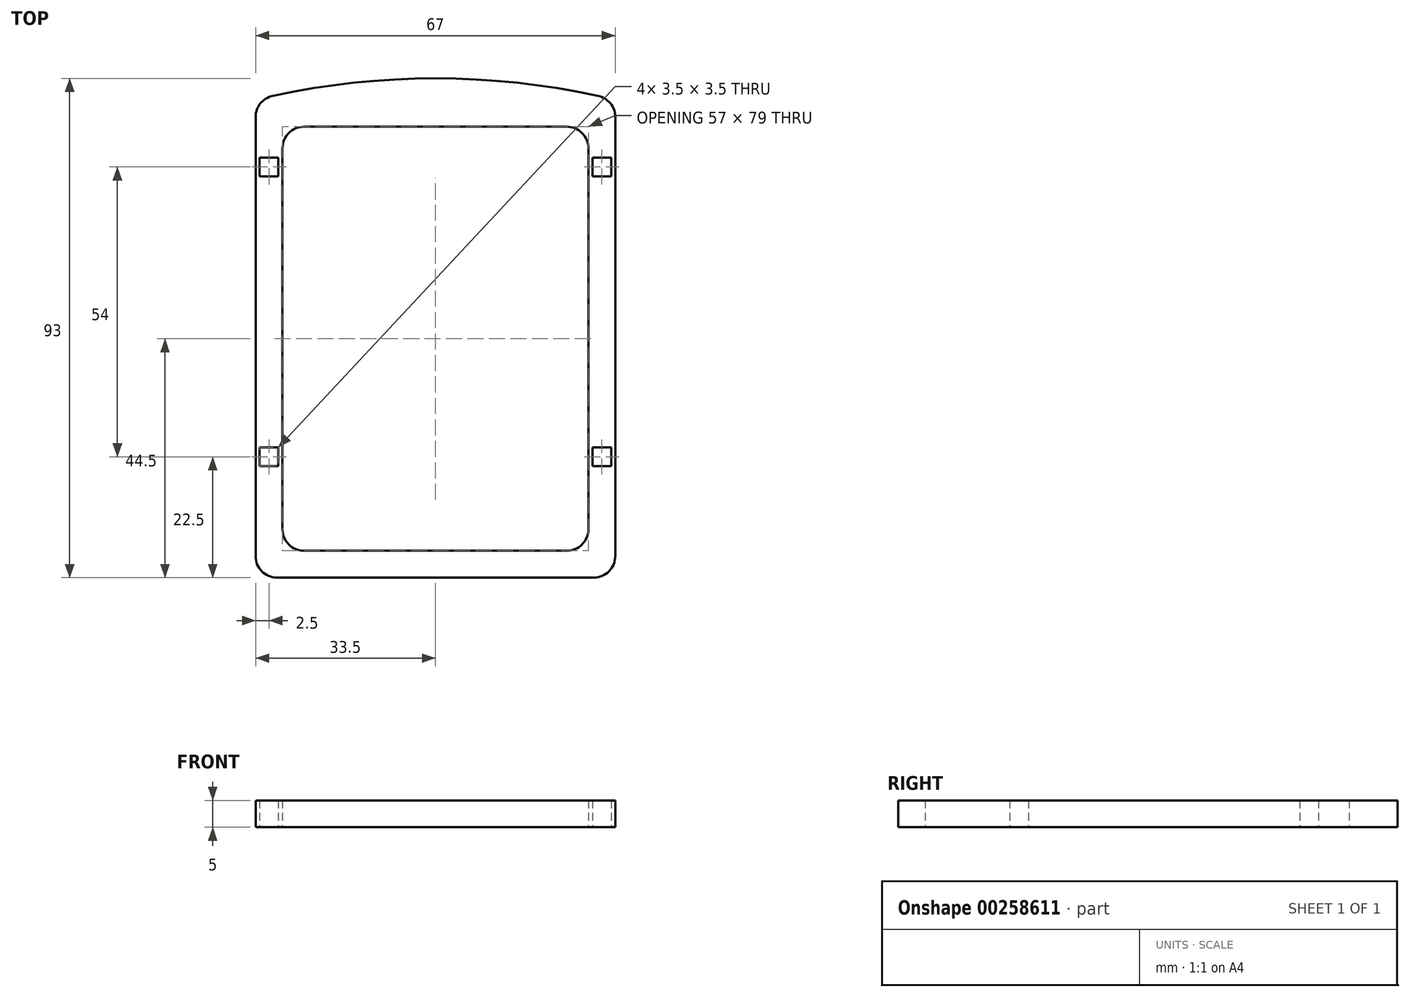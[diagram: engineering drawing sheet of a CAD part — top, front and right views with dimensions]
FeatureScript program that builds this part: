
annotation { "Feature Type Name" : "Feature", "Feature Type Description" : "" }
export const myFeature = defineFeature(function(context is Context, id is Id, definition is map)
    precondition{}
    {
        {
            var Q0;
            Q0=qCreatedBy(makeId("Top.planeOp"),FACE);
            var sketch = newSketch(context, id + "F0", { "sketchPlane" : qUnion([Q0])});
            skLineSegment(sketch, "E0.bottom", {"start": v(33.5, 44.5) * mm, "end": v(-33.5, 44.5) * mm});
            skLineSegment(sketch, "E0.top", {"start": v(33.5, -44.5) * mm, "end": v(-33.5, -44.5) * mm});
            skLineSegment(sketch, "E0.left", {"start": v(33.5, 44.5) * mm, "end": v(33.5, -44.5) * mm});
            skLineSegment(sketch, "E0.right", {"start": v(-33.5, 44.5) * mm, "end": v(-33.5, -44.5) * mm});
            skPoint(sketch, "E0.middle", {"position": v(0, 0) * mm});
            skLineSegment(sketch, "E1.0", {"start": v(-28.5, 39.5) * mm, "end": v(-28.5, -39.5) * mm});
            skLineSegment(sketch, "E1.1", {"start": v(28.5, 39.5) * mm, "end": v(-28.5, 39.5) * mm});
            skLineSegment(sketch, "E1.2", {"start": v(28.5, 39.5) * mm, "end": v(28.5, -39.5) * mm});
            skLineSegment(sketch, "E1.3", {"start": v(28.5, -39.5) * mm, "end": v(-28.5, -39.5) * mm});
            skLineSegment(sketch, "E2", {"start": v(0, -44.5) * mm, "end": v(0, 48.5) * mm, "construction": true});
            skPoint(sketch, "E2.endSnap0", {"position": v(0, -39.5) * mm});
            skArc(sketch, "E3", {"start": v(33.5, 44.5) * mm, "mid": v(0, 48.5) * mm, "end": v(-33.5, 44.5) * mm});
            skLineSegment(sketch, "E4.bottom", {"start": v(-28.5, 39.5) * mm, "end": v(-33.5, 39.5) * mm, "construction": true});
            skLineSegment(sketch, "E4.top", {"start": v(-28.5, 34.5) * mm, "end": v(-33.5, 34.5) * mm, "construction": true});
            skLineSegment(sketch, "E4.left", {"start": v(-28.5, 39.5) * mm, "end": v(-28.5, 34.5) * mm, "construction": true});
            skLineSegment(sketch, "E4.right", {"start": v(-33.5, 39.5) * mm, "end": v(-33.5, 34.5) * mm, "construction": true});
            skLineSegment(sketch, "E5.bottom", {"start": v(28.5, 39.5) * mm, "end": v(33.5, 39.5) * mm, "construction": true});
            skLineSegment(sketch, "E5.top", {"start": v(28.5, 34.5) * mm, "end": v(33.5, 34.5) * mm, "construction": true});
            skLineSegment(sketch, "E5.left", {"start": v(28.5, 39.5) * mm, "end": v(28.5, 34.5) * mm, "construction": true});
            skLineSegment(sketch, "E5.right", {"start": v(33.5, 39.5) * mm, "end": v(33.5, 34.5) * mm, "construction": true});
            skLineSegment(sketch, "E6.bottom", {"start": v(-33.5, 34.5) * mm, "end": v(-28.5, 34.5) * mm, "construction": true});
            skLineSegment(sketch, "E6.top", {"start": v(-33.5, 29.5) * mm, "end": v(-28.5, 29.5) * mm, "construction": true});
            skLineSegment(sketch, "E6.left", {"start": v(-33.5, 34.5) * mm, "end": v(-33.5, 29.5) * mm, "construction": true});
            skLineSegment(sketch, "E6.right", {"start": v(-28.5, 34.5) * mm, "end": v(-28.5, 29.5) * mm, "construction": true});
            skLineSegment(sketch, "E7.top", {"start": v(28.5, 29.5) * mm, "end": v(33.5, 29.5) * mm, "construction": true});
            skLineSegment(sketch, "E7.left", {"start": v(28.5, 34.5) * mm, "end": v(28.5, 29.5) * mm, "construction": true});
            skLineSegment(sketch, "E7.right", {"start": v(33.5, 34.5) * mm, "end": v(33.5, 29.5) * mm, "construction": true});
            skLineSegment(sketch, "E8.bottom", {"start": v(-29.25, 33.75) * mm, "end": v(-32.75, 33.75) * mm});
            skLineSegment(sketch, "E8.top", {"start": v(-29.25, 30.25) * mm, "end": v(-32.75, 30.25) * mm});
            skLineSegment(sketch, "E8.left", {"start": v(-29.25, 33.75) * mm, "end": v(-29.25, 30.25) * mm});
            skLineSegment(sketch, "E8.right", {"start": v(-32.75, 33.75) * mm, "end": v(-32.75, 30.25) * mm});
            skPoint(sketch, "E8.middle", {"position": v(-31, 32) * mm});
            skPoint(sketch, "E8.middle.positionSnap0", {"position": v(-28.5, 32) * mm});
            skPoint(sketch, "E8.middle.positionSnap1", {"position": v(-31, 29.5) * mm});
            skPoint(sketch, "E8.centerSnap0", {"position": v(-28.5, 32) * mm});
            skPoint(sketch, "E8.centerSnap1", {"position": v(-31, 29.5) * mm});
            skLineSegment(sketch, "E9.bottom", {"start": v(32.75, 33.75) * mm, "end": v(29.25, 33.75) * mm});
            skLineSegment(sketch, "E9.top", {"start": v(32.75, 30.25) * mm, "end": v(29.25, 30.25) * mm});
            skLineSegment(sketch, "E9.left", {"start": v(32.75, 33.75) * mm, "end": v(32.75, 30.25) * mm});
            skLineSegment(sketch, "E9.right", {"start": v(29.25, 33.75) * mm, "end": v(29.25, 30.25) * mm});
            skPoint(sketch, "E9.middle", {"position": v(31, 32) * mm});
            skPoint(sketch, "E9.middle.positionSnap0", {"position": v(28.5, 32) * mm});
            skPoint(sketch, "E9.middle.positionSnap1", {"position": v(31, 29.5) * mm});
            skPoint(sketch, "E9.centerSnap0", {"position": v(28.5, 32) * mm});
            skPoint(sketch, "E9.centerSnap1", {"position": v(31, 29.5) * mm});
            skLineSegment(sketch, "E10.bottom", {"start": v(-33.5, -44.5) * mm, "end": v(-28.5, -44.5) * mm, "construction": true});
            skLineSegment(sketch, "E10.top", {"start": v(-33.5, -24.5) * mm, "end": v(-28.5, -24.5) * mm, "construction": true});
            skLineSegment(sketch, "E10.left", {"start": v(-33.5, -44.5) * mm, "end": v(-33.5, -24.5) * mm, "construction": true});
            skLineSegment(sketch, "E10.right", {"start": v(-28.5, -44.5) * mm, "end": v(-28.5, -24.5) * mm, "construction": true});
            skLineSegment(sketch, "E11.bottom", {"start": v(33.5, -44.5) * mm, "end": v(28.5, -44.5) * mm, "construction": true});
            skLineSegment(sketch, "E11.top", {"start": v(33.5, -24.5) * mm, "end": v(28.5, -24.5) * mm, "construction": true});
            skLineSegment(sketch, "E11.left", {"start": v(33.5, -44.5) * mm, "end": v(33.5, -24.5) * mm, "construction": true});
            skLineSegment(sketch, "E11.right", {"start": v(28.5, -44.5) * mm, "end": v(28.5, -24.5) * mm, "construction": true});
            skLineSegment(sketch, "E12.bottom", {"start": v(-28.5, -24.5) * mm, "end": v(-33.5, -24.5) * mm, "construction": true});
            skLineSegment(sketch, "E12.top", {"start": v(-28.5, -19.5) * mm, "end": v(-33.5, -19.5) * mm, "construction": true});
            skLineSegment(sketch, "E12.left", {"start": v(-28.5, -24.5) * mm, "end": v(-28.5, -19.5) * mm, "construction": true});
            skLineSegment(sketch, "E12.right", {"start": v(-33.5, -24.5) * mm, "end": v(-33.5, -19.5) * mm, "construction": true});
            skLineSegment(sketch, "E13.bottom", {"start": v(28.5, -24.5) * mm, "end": v(33.5, -24.5) * mm, "construction": true});
            skLineSegment(sketch, "E13.top", {"start": v(28.5, -19.5) * mm, "end": v(33.5, -19.5) * mm, "construction": true});
            skLineSegment(sketch, "E13.left", {"start": v(28.5, -24.5) * mm, "end": v(28.5, -19.5) * mm, "construction": true});
            skLineSegment(sketch, "E13.right", {"start": v(33.5, -24.5) * mm, "end": v(33.5, -19.5) * mm, "construction": true});
            skLineSegment(sketch, "E14.bottom", {"start": v(-29.25, -20.25) * mm, "end": v(-32.75, -20.25) * mm});
            skLineSegment(sketch, "E14.top", {"start": v(-29.25, -23.75) * mm, "end": v(-32.75, -23.75) * mm});
            skLineSegment(sketch, "E14.left", {"start": v(-29.25, -20.25) * mm, "end": v(-29.25, -23.75) * mm});
            skLineSegment(sketch, "E14.right", {"start": v(-32.75, -20.25) * mm, "end": v(-32.75, -23.75) * mm});
            skPoint(sketch, "E14.middle", {"position": v(-31, -22) * mm});
            skPoint(sketch, "E14.middle.positionSnap0", {"position": v(-31, -24.5) * mm});
            skPoint(sketch, "E14.middle.positionSnap1", {"position": v(-28.5, -22) * mm});
            skPoint(sketch, "E14.centerSnap0", {"position": v(-31, -24.5) * mm});
            skPoint(sketch, "E14.centerSnap1", {"position": v(-28.5, -22) * mm});
            skLineSegment(sketch, "E15.bottom", {"start": v(32.75, -20.25) * mm, "end": v(29.25, -20.25) * mm});
            skLineSegment(sketch, "E15.top", {"start": v(32.75, -23.75) * mm, "end": v(29.25, -23.75) * mm});
            skLineSegment(sketch, "E15.left", {"start": v(32.75, -20.25) * mm, "end": v(32.75, -23.75) * mm});
            skLineSegment(sketch, "E15.right", {"start": v(29.25, -20.25) * mm, "end": v(29.25, -23.75) * mm});
            skPoint(sketch, "E15.middle", {"position": v(31, -22) * mm});
            skPoint(sketch, "E15.middle.positionSnap0", {"position": v(28.5, -22) * mm});
            skPoint(sketch, "E15.middle.positionSnap1", {"position": v(31, -24.5) * mm});
            skPoint(sketch, "E15.centerSnap0", {"position": v(28.5, -22) * mm});
            skPoint(sketch, "E15.centerSnap1", {"position": v(31, -24.5) * mm});
            skSolve(sketch);
        }
        {
            var Q0;
            Q0=makeQuery(id+"F0.imprint","IMPRINT",FACE,{"disambiguationData":[TD([[makeQuery(id+"F0.imprint","IMPRINT",EDGE,{"derivedFrom":sQuery(id+"F0.wireOp",EDGE,"E0.bottom")}),1.0]])]});
            var Q1;
            Q1=makeQuery(id+"F0.imprint","IMPRINT",FACE,{"disambiguationData":[TD([[makeQuery(id+"F0.imprint","IMPRINT",EDGE,{"derivedFrom":sQuery(id+"F0.wireOp",EDGE,"E0.bottom")}),-1.0]])]});
            extrude(context, id + "F1", {"entities" : qUnion([Q0, Q1]), "depth" : 5 * mm});
        }
        {
            var Q0;
            Q0=makeQuery(id+"F1.opExtrude","SWEPT_EDGE",EDGE,{"disambiguationData":[OSD([sQuery(id+"F0.wireOp",EDGE,"E0.top"),sQuery(id+"F0.wireOp",EDGE,"E0.right")])]});
            var Q1;
            Q1=makeQuery(id+"F1.opExtrude","SWEPT_EDGE",EDGE,{"disambiguationData":[OSD([sQuery(id+"F0.wireOp",EDGE,"E0.top"),sQuery(id+"F0.wireOp",EDGE,"E0.left")])]});
            var Q2;
            Q2=makeQuery(id+"F1.opExtrude","SWEPT_EDGE",EDGE,{"disambiguationData":[OSD([sQuery(id+"F0.wireOp",EDGE,"E0.bottom"),sQuery(id+"F0.wireOp",EDGE,"E0.right"),sQuery(id+"F0.wireOp",EDGE,"E3")])]});
            var Q3;
            Q3=makeQuery(id+"F1.opExtrude","SWEPT_EDGE",EDGE,{"disambiguationData":[OSD([sQuery(id+"F0.wireOp",EDGE,"E0.bottom"),sQuery(id+"F0.wireOp",EDGE,"E0.left"),sQuery(id+"F0.wireOp",EDGE,"E3")])]});
            var Q4;
            Q4=makeQuery(id+"F1.opExtrude","SWEPT_EDGE",EDGE,{"disambiguationData":[OSD([sQuery(id+"F0.wireOp",EDGE,"E1.0"),sQuery(id+"F0.wireOp",EDGE,"E1.1")])]});
            var Q5;
            Q5=makeQuery(id+"F1.opExtrude","SWEPT_EDGE",EDGE,{"disambiguationData":[OSD([sQuery(id+"F0.wireOp",EDGE,"E1.1"),sQuery(id+"F0.wireOp",EDGE,"E1.2")])]});
            var Q6;
            Q6=makeQuery(id+"F1.opExtrude","SWEPT_EDGE",EDGE,{"disambiguationData":[OSD([sQuery(id+"F0.wireOp",EDGE,"E1.2"),sQuery(id+"F0.wireOp",EDGE,"E1.3")])]});
            var Q7;
            Q7=makeQuery(id+"F1.opExtrude","SWEPT_EDGE",EDGE,{"disambiguationData":[OSD([sQuery(id+"F0.wireOp",EDGE,"E1.0"),sQuery(id+"F0.wireOp",EDGE,"E1.3")])]});
            fillet(context, id + "F2", {"entities" : qUnion([Q0, Q1, Q2, Q3, Q4, Q5, Q6, Q7]), "radius" : 4 * mm, "tangentPropagation" : true, "allowEdgeOverflow" : false});
        }
    });
